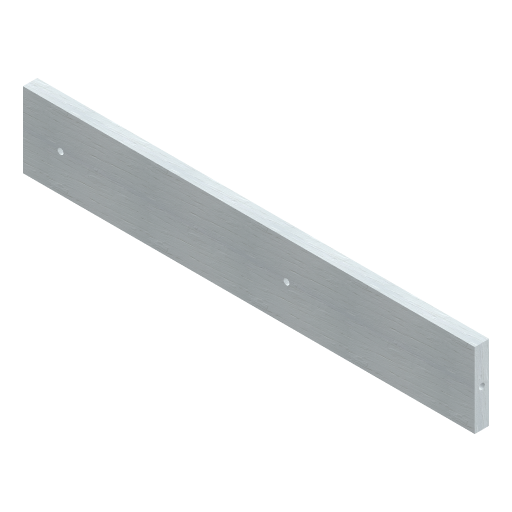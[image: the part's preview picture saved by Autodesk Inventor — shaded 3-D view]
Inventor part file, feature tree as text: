
AUTODESK INVENTOR PART (.ipt)
format: ipt  version: 2024 (Build 280153000, 153)  size: 207,872 bytes
history: native  units: in
note: dims shown in document units (in); Inventor stores cm internally (conversion verified against a paired STEP export)
features: extrude x5, sketch x5
ambient origin geometry x8: Origin, YZ Plane, XZ Plane, XY Plane, X Axis, Y Axis, Z Axis, Center Point
bodies: Solid1 (feature_tree)
feature tree (10):
  extrude  "Extrusion1"  Depth=3.937in
  extrude  "Extrusion2"  Depth=9.8425in
  extrude  "Extrusion3"  Depth=0.315in
  extrude  "Extrusion4"  Depth=0.4331in TaperAngle=0.0deg
  extrude  "Extrusion5"  Depth=0.4331in TaperAngle=0.0deg
  sketch  "Sketch1"  dims[d0=23.622in d1=3.937in]
  sketch  "Sketch2"  dims[d2=0.374in d3=0.374in d4=0.0in d5=0.0in d6=9.8425in]
  sketch  "Sketch3"  dims[d7=1.9685in d8=0.315in]
  sketch  "Sketch4"  dims[d9=0.315in d10=0.4331in d11=0.0in]
  sketch  "Sketch5"  dims[d12=0.315in d13=0.4331in d14=0.0in d15=0.315in d16=0.4331in d17=0.0in d18=1.9685in d19=6.5617in d20=6.5617in d21=6.5617in d22=1.9685in d23=0.315in d24=0.315in d25=0.315in d26=0.315in d27=0.4331in d28=0.0in]
